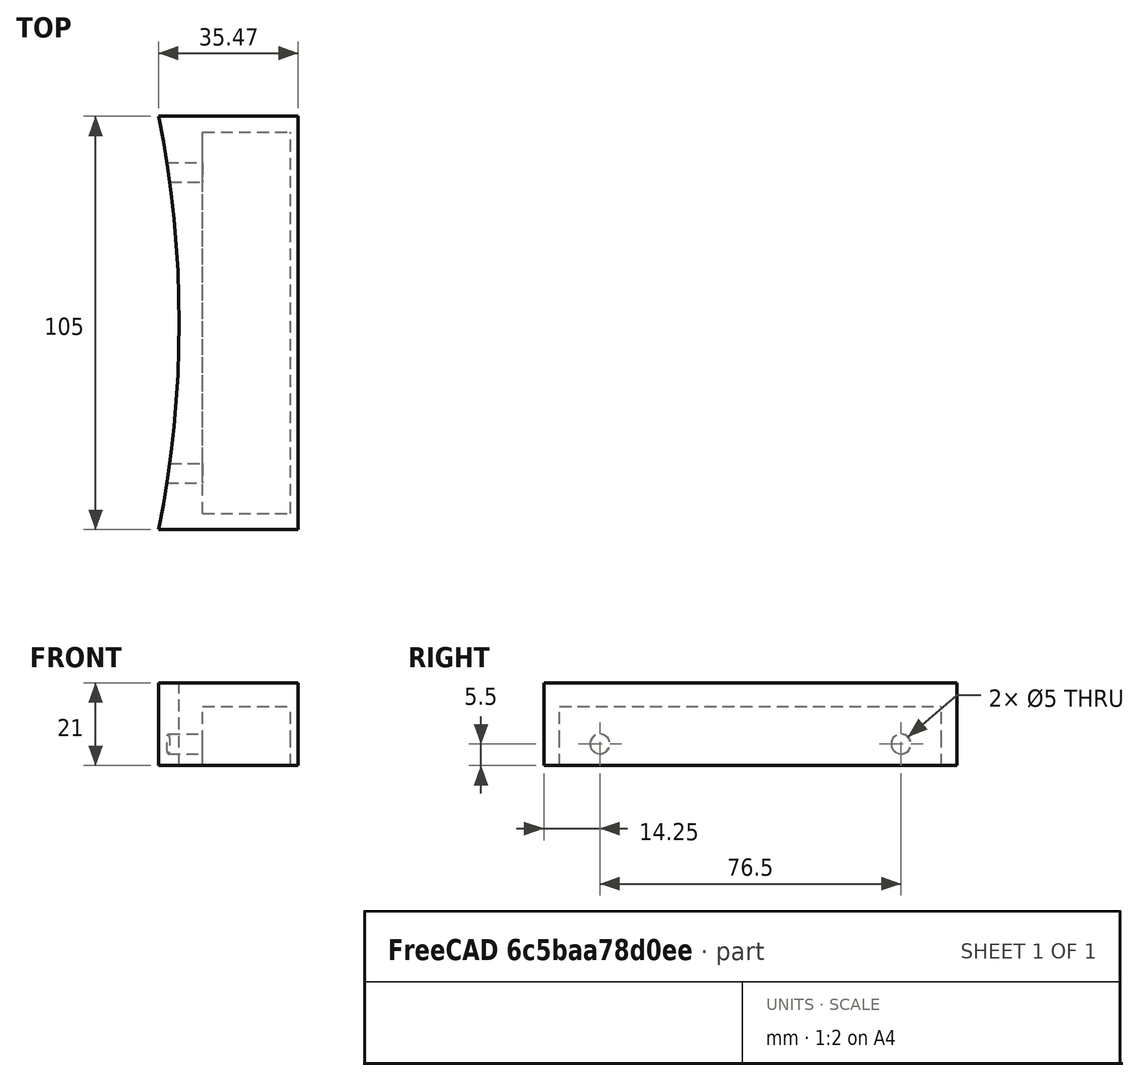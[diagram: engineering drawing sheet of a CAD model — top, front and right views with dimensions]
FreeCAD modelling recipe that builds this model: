
FCSTD DOCUMENT  (FreeCAD 0.16RUnknown)
Label: washerhandle
License: All rights reserved
LicenseURL: http://en.wikipedia.org/wiki/All_rights_reserved
objects: Part::FeaturePython×5, Part::Box×3, Part::Cylinder×3
note: 11 computed .brp shape members not serialized (recipe doc carries the construction recipe); baked Part::Feature solids carry a one-line shape summary decoded from their .brp

FEATURE [Part::Box] Box  label="body"
  Height = 42.25
  Length = 21
  Placement = pos=(30.25,-52.5,0) rot=(0,-1,0;1.5708rad)
  Width = 105
  expr: Placement.Base.x = 22.25 + 2 * 4
  expr: Height = 12 + 22.25 + 2 * 4
  expr: Placement.Base.y = -105 / 2
FEATURE [Part::Cylinder] Cylinder  label="ScrewHole1"
  Angle = 360
  Height = 17
  Placement = pos=(-10,-38.25,5.5) rot=(0,1,0;1.5708rad)
  Radius = 2.5
  expr: Placement.Base.z = 3 + 2.5
  expr: Placement.Base.y = 14.25 - 105 / 2
FEATURE [Part::Cylinder] Cylinder001  label="ScrewHole2"
  Angle = 360
  Height = 17
  Placement = pos=(-10,38.25,5.5) rot=(0,1,0;1.5708rad)
  Radius = 2.5
  expr: Placement.Base.z = 3 + 2.5
  expr: Placement.Base.y = 105 - 14.25 - 105 / 2
FEATURE [Part::Cylinder] Cylinder002  label="WasherDoor"
  Angle = 45
  Height = 21
  Placement = pos=(-266.7,0,0) rot=(0,0,-1;0.392699rad)
  Radius = 266.7
  expr: Radius = 533.4 / 2
FEATURE [Part::Box] Box001  label="handle"
  Height = 11
  Length = 22.25
  Placement = pos=(6,-48.5,-5) rot=(0,0,1;0rad)
  Width = 97
  expr: Height = 5 + 12 - 6
  expr: Placement.Base.y = -97 / 2
  expr: Width = 105 - 2 * 4
FEATURE [Part::FeaturePython] Cutout  # WARN: FeaturePython — macro-defined, semantics opaque (R4)
  Base = -> Box
  Mode = 3
  Tool = -> Cylinder002
FEATURE [Part::FeaturePython] Cutout001  # WARN: FeaturePython — macro-defined, semantics opaque (R4)
  Base = -> Cutout
  Mode = 3
  Tool = -> Box001
FEATURE [Part::FeaturePython] Cutout002  # WARN: FeaturePython — macro-defined, semantics opaque (R4)
  Base = -> Cutout001
  Mode = 3
  Tool = -> Cylinder
FEATURE [Part::FeaturePython] Cutout003  # WARN: FeaturePython — macro-defined, semantics opaque (R4)
  Base = -> Cutout002
  Mode = 3
  Tool = -> Cylinder001
FEATURE [Part::Box] Box002  label="Cube"
  Height = 15
  Length = 22.25
  Placement = pos=(6,-48.5,0) rot=(0,0,1;0rad)
  Width = 97
  expr: Placement.Base.y = -97 / 2
  expr: Width = 105 - 8
FEATURE [Part::FeaturePython] Cutout004  # WARN: FeaturePython — macro-defined, semantics opaque (R4)
  Base = -> Cutout003
  Mode = 3
  Tool = -> Box002
